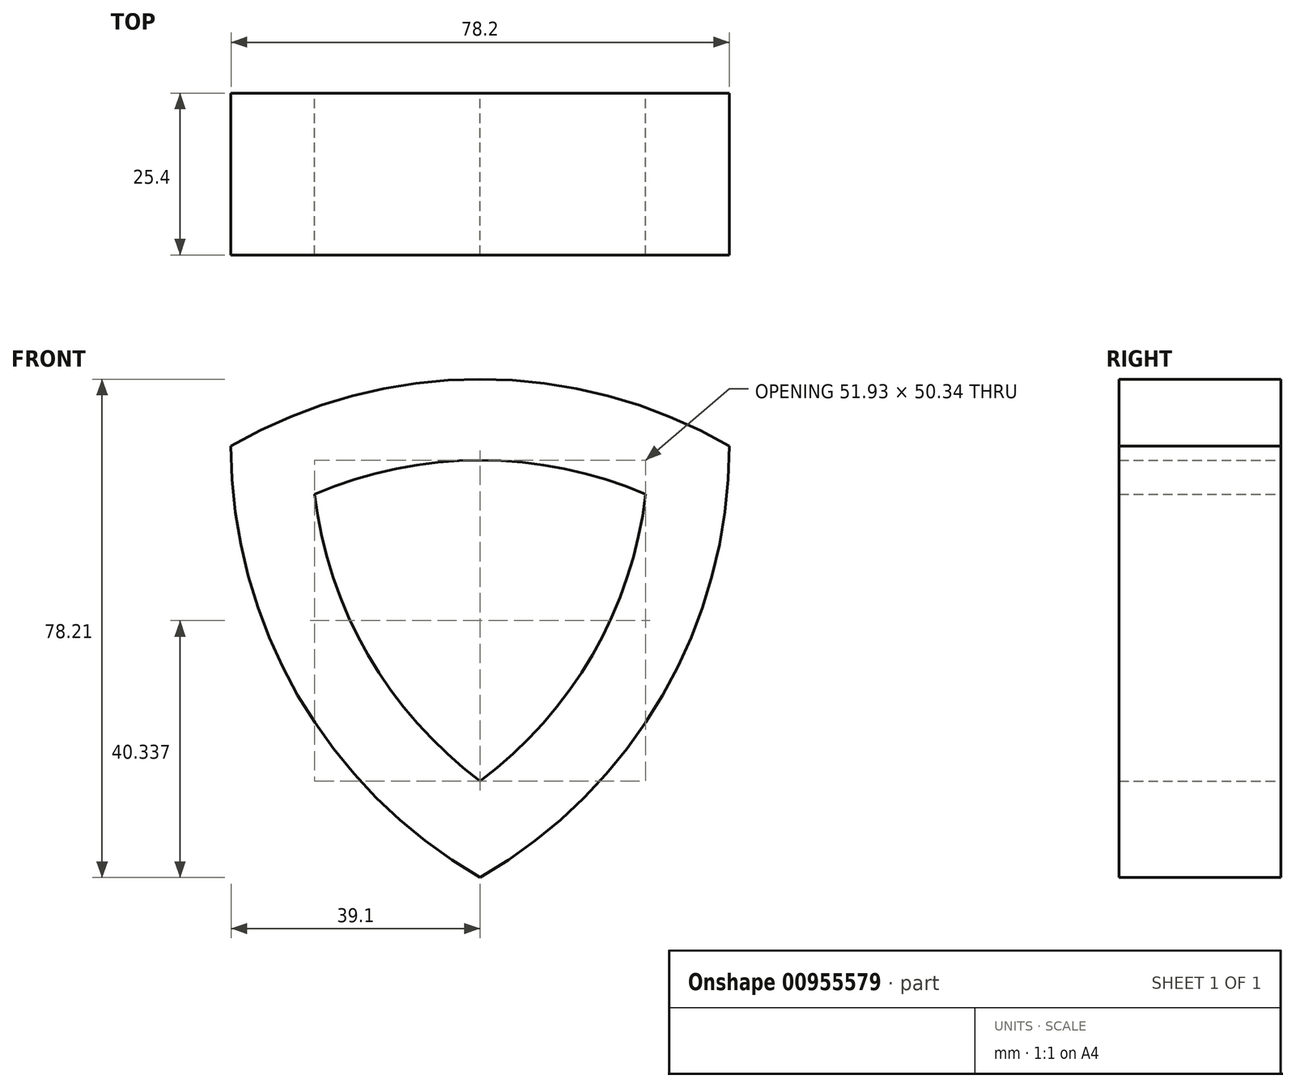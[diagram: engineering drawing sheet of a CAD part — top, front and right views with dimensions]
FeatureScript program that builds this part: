
annotation { "Feature Type Name" : "Feature", "Feature Type Description" : "" }
export const myFeature = defineFeature(function(context is Context, id is Id, definition is map)
    precondition{}
    {
        {
            var Q0;
            Q0=qCreatedBy(makeId("Front.planeOp"),FACE);
            var sketch = newSketch(context, id + "F0", { "sketchPlane" : qUnion([Q0])});
            skCircle(sketch, "E0.cCircle", {"center": v(0, 0) * mm, "radius": 22.58 * mm, "construction": true});
            skLineSegment(sketch, "E0.0", {"start": v(-39.1, 22.58) * mm, "end": v(39.1, 22.58) * mm, "construction": true});
            skLineSegment(sketch, "E0.1", {"start": v(39.1, 22.58) * mm, "end": v(0, -45.15) * mm, "construction": true});
            skLineSegment(sketch, "E0.2", {"start": v(0, -45.15) * mm, "end": v(-39.1, 22.58) * mm, "construction": true});
            skPoint(sketch, "E0.0.midPoint", {"position": v(0, 22.58) * mm});
            skArc(sketch, "E1", {"start": v(0, -45.15) * mm, "mid": v(28.63, -16.53) * mm, "end": v(39.1, 22.58) * mm});
            skArc(sketch, "E2", {"start": v(-39.1, 22.58) * mm, "mid": v(-28.63, -16.53) * mm, "end": v(0, -45.15) * mm});
            skArc(sketch, "E3", {"start": v(39.1, 22.58) * mm, "mid": v(0, 33.06) * mm, "end": v(-39.1, 22.58) * mm});
            skSolve(sketch);
        }
        {
            var Q0;
            Q0 = qSketchRegion(id + "F0", true);
            extrude(context, id + "F1", {"entities" : qUnion([Q0]), "depth" : 25.4 * mm, "offsetDistance" : 25.4 * mm});
        }
        {
            var Q0;
            Q0=makeQuery(id+"F1.opExtrude","CAP_FACE",FACE,{"disambiguationData":[OSD([sQuery(id+"F0.wireOp",EDGE,"E1"),sQuery(id+"F0.wireOp",EDGE,"E2"),sQuery(id+"F0.wireOp",EDGE,"E3")])],"isStart":false});
            var Q1;
            Q1=makeQuery(id+"F1.opExtrude","CAP_FACE",FACE,{"disambiguationData":[OSD([sQuery(id+"F0.wireOp",EDGE,"E1"),sQuery(id+"F0.wireOp",EDGE,"E2"),sQuery(id+"F0.wireOp",EDGE,"E3")])],"isStart":true});
            shell(context, id + "F2", {"entities" : qUnion([Q0, Q1]), "thickness" : 12.7 * mm});
        }
    });
